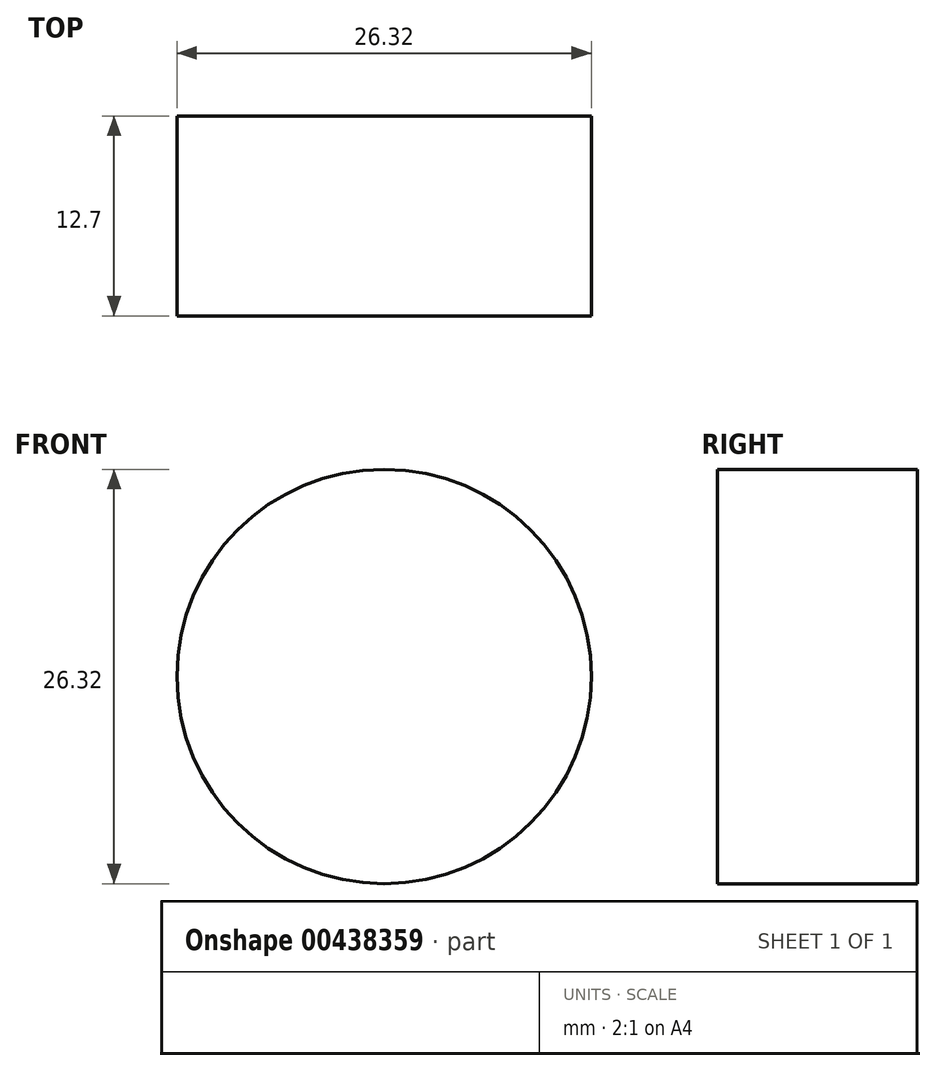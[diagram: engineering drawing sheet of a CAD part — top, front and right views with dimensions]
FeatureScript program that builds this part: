
annotation { "Feature Type Name" : "Feature", "Feature Type Description" : "" }
export const myFeature = defineFeature(function(context is Context, id is Id, definition is map)
    precondition{}
    {
        {
            var Q0;
            Q0=qCreatedBy(makeId("Front.planeOp"),FACE);
            var sketch = newSketch(context, id + "F0", { "sketchPlane" : qUnion([Q0])});
            skCircle(sketch, "E0", {"center": v(0, 0) * mm, "radius": 13.16 * mm});
            skSolve(sketch);
        }
        {
            var Q0;
            Q0 = qSketchRegion(id + "F0", true);
            extrude(context, id + "F1", {"entities" : qUnion([Q0]), "depth" : 12.7 * mm});
        }
    });
